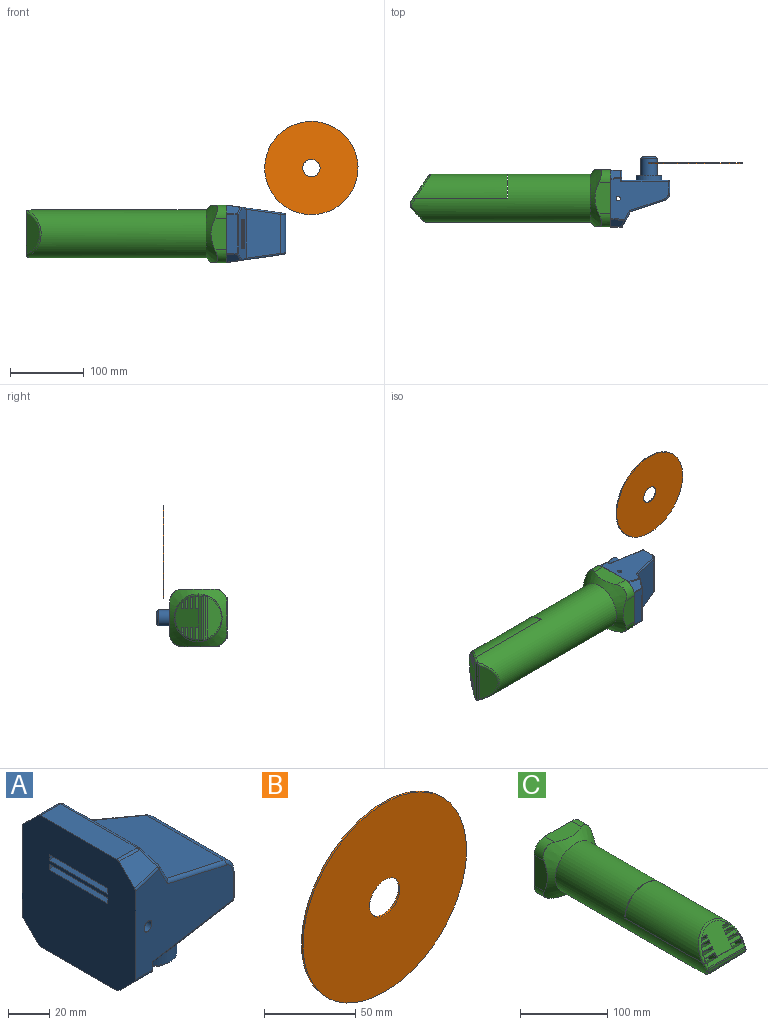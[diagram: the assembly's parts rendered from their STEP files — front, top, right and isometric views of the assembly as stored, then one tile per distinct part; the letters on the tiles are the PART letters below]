
ASSEMBLY  parts=3 mates=1
PART A: 66 faces, bbox 80.5x78.2x96.5 mm
  f0: plane 51.53x15.56mm, normal (1,0,0), area 801.8mm2, adj f22,f50,f56,f59
  f1: plane 68.69x20.14mm, normal (0.88,0,0.48), area 1249.5mm2, adj f4,f12,f13,f14,f15,f16,f17,f18
  f2: plane 70.22x12.02mm, normal (1,0,0), area 762.8mm2, adj f3,f33,f34,f44,f45,f49,f52,f55
  f3: plane 69.65x63mm, normal (0,0,-1), area 2855.1mm2, adj f2,f49,f55,f56,f61
  f4: plane 66.47x46.27mm, normal (0.32,0,0.95), area 2918.6mm2, adj f1,f22,f40,f54
  f5: plane 13x10.81mm, normal (0,-0.71,-0.71), area 181.5mm2, adj f7,f24,f34,f35
  f6: plane 18.33x10.81mm, normal (0,-0.71,0.71), area 219.9mm2, adj f7,f23,f25,f26
  f7: plane 78.03x78.03mm, normal (-1,0,0), area 5521.2mm2, adj f5,f6,f8,f9,f10,f11,f12,f13
  f8: plane 52.34x13.82mm, normal (0,0,1), area 723.3mm2, adj f7,f23,f30,f31
  f9: plane 52.34x13mm, normal (0,0,-1), area 680.5mm2, adj f7,f24,f32,f33
  f10: plane 13x10.81mm, normal (0,0.71,-0.71), area 181.5mm2, adj f7,f32,f43,f44
  f11: plane 18.33x10.81mm, normal (0,0.71,0.71), area 219.9mm2, adj f7,f31,f41,f42
  f12: plane 40x20.07mm, normal (0.48,0,-0.88), area 917.1mm2, adj f1,f7,f13,f15
  f13: plane 21.52x14.5mm, normal (0,1,0), area 71.3mm2, adj f1,f7,f12,f14
  f14: plane 40x21.52mm, normal (-0.48,0,0.88), area 983.3mm2, adj f1,f7,f13,f15
  f15: plane 21.52x14.5mm, normal (0,-1,0), area 71.3mm2, adj f1,f7,f12,f14
  f16: plane 40x22.47mm, normal (0.48,0,-0.88), area 1026.4mm2, adj f1,f7,f17,f19
  f17: plane 23.92x15.82mm, normal (0,1,0), area 79.5mm2, adj f1,f7,f16,f18
  f18: plane 40x23.92mm, normal (-0.48,0,0.88), area 1092.6mm2, adj f1,f7,f17,f19
  f19: plane 23.92x15.82mm, normal (0,-1,0), area 79.5mm2, adj f1,f7,f16,f18
  f20: plane 78.47x57.07mm, normal (0.14,0.99,0), area 2906.3mm2, adj f7,f42,f43,f51,f52,f54,f55,f57
  f21: plane 78.28x56.89mm, normal (0.14,-0.99,0), area 2906.3mm2, adj f7,f25,f35,f36,f40,f45,f46,f49
  f22: cylinder r=10.34mm len=53.17mm, axis (0,1,0), area 672.2mm2, adj f0,f4,f46,f57
  f23: cylinder r=2mm len=13.82mm, axis (1,0,0), area 21.7mm2, adj f6,f7,f8,f27
  f24: cylinder r=2mm len=13mm, axis (-1,0,0), area 20.4mm2, adj f5,f7,f9,f28
  f25: cylinder r=2mm len=18.9mm, axis (0.98,0.14,0.14), area 30mm2, adj f6,f7,f21,f29
  f26: cylinder r=2mm len=9.59mm, axis (-0.36,0.66,0.66), area 30.3mm2, adj f1,f6,f27,f29
  f27: sphere r=2mm, area 1.9mm2, adj f23,f26,f30
  f28: sphere r=2mm, area 3.1mm2, adj f24,f33,f34
  f29: sphere r=2mm, area 2.4mm2, adj f25,f26,f36
  f30: cylinder r=2mm len=52.34mm, axis (0,1,0), area 111.7mm2, adj f1,f8,f27,f37
  f31: cylinder r=2mm len=13.82mm, axis (1,0,0), area 21.7mm2, adj f7,f8,f11,f37
  f32: cylinder r=2mm len=13mm, axis (-1,0,0), area 20.4mm2, adj f7,f9,f10,f38
  f33: cylinder r=2mm len=52.34mm, axis (0,1,0), area 164.4mm2, adj f2,f9,f28,f38
  f34: cylinder r=2mm len=10.35mm, axis (0,-0.71,0.71), area 39.7mm2, adj f2,f5,f28,f39
  f35: cylinder r=2mm len=13.57mm, axis (0.98,0.14,-0.14), area 21.3mm2, adj f5,f7,f21,f39
  f36: cylinder r=2mm len=13.6mm, axis (0.48,0.07,-0.87), area 40.5mm2, adj f1,f21,f29,f40
  f37: sphere r=2mm, area 1.9mm2, adj f30,f31,f41
  f38: sphere r=2mm, area 3.1mm2, adj f32,f33,f44
  f39: sphere r=2mm, area 2.9mm2, adj f34,f35,f45
  f40: cylinder r=2mm len=47.41mm, axis (0.94,0.14,-0.31), area 151.2mm2, adj f1,f4,f21,f36,f46
  f41: cylinder r=2mm len=9.59mm, axis (-0.36,-0.66,0.66), area 30.3mm2, adj f1,f11,f37,f47
  f42: cylinder r=2mm len=18.9mm, axis (0.98,-0.14,0.14), area 30mm2, adj f7,f11,f20,f47
  f43: cylinder r=2mm len=13.57mm, axis (0.98,-0.14,-0.14), area 21.3mm2, adj f7,f10,f20,f48
  f44: cylinder r=2mm len=10.35mm, axis (0,0.71,0.71), area 39.7mm2, adj f2,f10,f38,f48
  f45: cylinder r=2mm len=5.06mm, axis (0,0,-1), area 11mm2, adj f2,f21,f39,f49
  f46: bspline ~9.8x7.41mm, area 35mm2, adj f21,f22,f40,f50
  f47: sphere r=2mm, area 2.4mm2, adj f41,f42,f51
  f48: sphere r=2mm, area 2.9mm2, adj f43,f44,f52
  f49: cylinder r=2mm len=65.28mm, axis (-0.99,-0.14,0), area 202.3mm2, adj f2,f3,f21,f45,f53
  f50: cylinder r=2mm len=15.56mm, axis (0,0,-1), area 44.4mm2, adj f0,f21,f46,f53
  f51: cylinder r=2mm len=13.6mm, axis (-0.48,0.07,0.87), area 40.5mm2, adj f1,f20,f47,f54
  f52: cylinder r=2mm len=5.06mm, axis (0,0,1), area 11mm2, adj f2,f20,f48,f55
  f53: sphere r=2mm, area 5.7mm2, adj f49,f50,f56
  f54: cylinder r=2mm len=47.41mm, axis (-0.94,0.14,0.31), area 151.2mm2, adj f1,f4,f20,f51,f57
  f55: cylinder r=2mm len=65.28mm, axis (0.99,-0.14,0), area 202.3mm2, adj f2,f3,f20,f52,f58
  f56: cylinder r=2mm len=51.53mm, axis (0,-1,0), area 161.9mm2, adj f0,f3,f53,f58
  f57: bspline ~9.8x7.41mm, area 35mm2, adj f20,f22,f54,f59
  f58: sphere r=2mm, area 5.7mm2, adj f55,f56,f59
  f59: cylinder r=2mm len=15.56mm, axis (0,0,1), area 44.4mm2, adj f0,f20,f57,f58
  f60: cylinder r=3.04mm len=76.01mm, axis (0,1,0), area 1434.7mm2, adj f20,f21
  f61: cylinder r=17.5mm len=35mm, axis (0,0,1), area 769.7mm2, adj f3,f62
  f62: plane 35x35mm, normal (0,0,-1), area 582mm2, adj f61,f63
  f63: cylinder r=11mm len=23.3mm, axis (0,0,1), area 1610.4mm2, adj f62,f65
  f64: plane 18x18mm, normal (0,0,-1), area 254.5mm2, adj f65
  f65: cone r=9mm half-angle=45deg, axis (0,0,1), area 177.7mm2, adj f63,f64
PART B: 4 faces, bbox 126.9x1.2x126.9 mm
  f0: cylinder r=11.79mm len=23.58mm, axis (0,1,0), area 88.9mm2, adj f2,f3
  f1: cylinder r=63.44mm len=126.87mm, axis (0,1,0), area 478.3mm2, adj f2,f3
  f2: plane 126.87x126.87mm, normal (0,-1,0), area 12205.9mm2, adj f0,f1
  f3: plane 126.87x126.87mm, normal (0,1,0), area 12205.9mm2, adj f0,f1
PART C: 123 faces, bbox 95.5x277.8x95.5 mm
  f0: plane 58.88x5.05mm, normal (0,-0.82,0.57), area 333.3mm2, adj f1,f2,f9,f11,f23,f35,f46,f111
  f1: bspline ~16.85x12.86mm, area 47.4mm2, adj f0,f10,f18,f19,f22,f23,f46,f111
  f2: bspline ~16.85x12.86mm, area 47.4mm2, adj f0,f12,f18,f19,f22,f23,f35,f111
  f3: cylinder r=42.74mm len=15.09mm, axis (0,-0.82,0.57), area 67.1mm2, adj f4,f12,f35,f39,f111
  f4: plane 16.41x6.55mm, normal (0,-0.57,-0.82), area 131.3mm2, adj f3,f5,f39,f111
  f5: plane 15.13x9.21mm, normal (1,0,0), area 67.1mm2, adj f4,f11,f35,f39,f111
  f6: cylinder r=42.74mm len=15.09mm, axis (0,-0.82,0.57), area 67.1mm2, adj f8,f10,f46,f49,f111
  f7: plane 15.13x9.21mm, normal (-1,0,0), area 67.1mm2, adj f8,f9,f46,f49,f111
  f8: plane 16.41x6.55mm, normal (0,-0.57,-0.82), area 131.3mm2, adj f6,f7,f49,f111
  f9: cylinder r=0.48mm len=1.16mm, axis (0,0.57,0.82), area 0.7mm2, adj f0,f7,f46,f111
  f10: bspline ~4.96x3.72mm, area 0.8mm2, adj f1,f6,f46,f111
  f11: cylinder r=0.48mm len=1.16mm, axis (0,-0.57,-0.82), area 0.7mm2, adj f0,f5,f35,f111
  f12: bspline ~4.96x3.72mm, area 0.8mm2, adj f2,f3,f35,f111
  f13: plane 58.81x31.18mm, normal (0,-0.82,0.57), area 1321.5mm2, adj f14,f43,f51,f58,f63,f68,f71,f75
  f14: bspline ~65x34.27mm, area 379.4mm2, adj f13,f18,f43,f51,f58,f63,f68,f71
  f15: plane 6.23x6.23mm, normal (0,-1,0), area 2.1mm2, adj f31,f34
  f16: plane 6.23x6.23mm, normal (0,-1,0), area 2.1mm2, adj f30,f34
  f17: plane 6.23x6.23mm, normal (0,-1,0), area 2.1mm2, adj f33,f34
  f18: cylinder r=32.5mm len=243.48mm, axis (0,1,0), area 46579.7mm2, adj f1,f2,f14,f22,f34,f109,f110,f111
  f19: plane 61.71x3.98mm, normal (0,-1,0), area 226.9mm2, adj f1,f2,f21,f22,f23
  f20: plane 55.12x18.98mm, normal (0,-0.73,-0.68), area 1034.3mm2, adj f21,f22
  f21: cylinder r=3mm len=60.35mm, axis (1,0,0), area 129.2mm2, adj f19,f20,f22
  f22: bspline ~62.38x23.36mm, area 276.2mm2, adj f1,f2,f18,f19,f20,f21
  f23: cylinder r=3mm len=60.2mm, axis (-1,0,0), area 107.7mm2, adj f0,f1,f2,f19
  f24: plane 42.75x21.71mm, normal (1,0,0), area 847.7mm2, adj f28,f30,f33,f34
  f25: plane 42.75x21.71mm, normal (0,0,1), area 847.7mm2, adj f28,f30,f31,f34
  f26: plane 42.75x21.71mm, normal (-1,0,0), area 847.7mm2, adj f28,f31,f32,f34
  f27: plane 42.75x21.71mm, normal (0,0,-1), area 847.7mm2, adj f28,f32,f33,f34
  f28: plane 78x78mm, normal (0,1,0), area 5817.4mm2, adj f24,f25,f26,f27,f30,f31,f32,f33
  f29: plane 6.23x6.23mm, normal (0,-1,0), area 2.1mm2, adj f32,f34
  f30: cylinder r=17.62mm len=17.62mm, axis (0,1,0), area 393.8mm2, adj f16,f24,f25,f28,f34
  f31: cylinder r=17.62mm len=17.62mm, axis (0,-1,0), area 393.8mm2, adj f15,f25,f26,f28,f34
  f32: cylinder r=17.62mm len=17.62mm, axis (0,1,0), area 393.8mm2, adj f26,f27,f28,f29,f34
  f33: cylinder r=17.62mm len=17.62mm, axis (0,-1,0), area 393.8mm2, adj f17,f24,f27,f28,f34
  f34: cone r=32.5mm half-angle=45deg, axis (0,1,0), area 3495.9mm2, adj f15,f16,f17,f18,f24,f25,f26,f27
  f35: plane 17.5x12.31mm, normal (0,0.57,0.82), area 246.3mm2, adj f0,f2,f3,f5,f11,f12,f39
  f36: cylinder r=42.74mm len=7.69mm, axis (0,-0.82,0.57), area 13.9mm2, adj f37,f83,f84,f110
  f37: plane 16.41x5.2mm, normal (0,-0.57,-0.82), area 104.1mm2, adj f36,f38,f81,f82,f84,f110
  f38: plane 7.75x3.64mm, normal (1,0,0), area 14.1mm2, adj f37,f80,f110
  f39: plane 16.51x4.62mm, normal (0,-0.82,0.57), area 93mm2, adj f3,f4,f5,f35
  f40: cylinder r=28.27mm len=13.96mm, axis (0,-0.82,0.57), area 58.5mm2, adj f41,f43,f44,f92
  f41: plane 11.94x11.89mm, normal (0,-0.57,-0.82), area 173.3mm2, adj f40,f42,f44,f90,f91,f92
  f42: plane 14x11.34mm, normal (1,0,0), area 53.4mm2, adj f41,f43,f44,f89
  f43: plane 14.71x12.3mm, normal (0,0.57,0.82), area 204.2mm2, adj f13,f14,f40,f42,f44,f89,f92
  f44: plane 13.6x3.01mm, normal (0,-0.82,0.57), area 47.1mm2, adj f40,f41,f42,f43
  f45: cylinder r=42.74mm len=7.69mm, axis (0,-0.82,0.57), area 13.9mm2, adj f48,f78,f79,f110
  f46: plane 17.5x12.31mm, normal (0,0.57,0.82), area 246.3mm2, adj f0,f1,f6,f7,f9,f10,f49
  f47: plane 7.75x3.64mm, normal (-1,0,0), area 14.1mm2, adj f48,f75,f110
  f48: plane 16.41x5.2mm, normal (0,-0.57,-0.82), area 104.1mm2, adj f45,f47,f76,f77,f79,f110
  f49: plane 16.51x4.62mm, normal (0,-0.82,0.57), area 93mm2, adj f6,f7,f8,f46
  f50: cylinder r=28.27mm len=13.96mm, axis (0,-0.82,0.57), area 58.5mm2, adj f51,f53,f54,f88
  f51: plane 14.71x12.3mm, normal (0,0.57,0.82), area 204.2mm2, adj f13,f14,f50,f52,f54,f85,f88
  f52: plane 14x11.34mm, normal (-1,0,0), area 53.4mm2, adj f51,f53,f54,f85
  f53: plane 11.94x11.89mm, normal (0,-0.57,-0.82), area 173.3mm2, adj f50,f52,f54,f86,f87,f88
  f54: plane 13.6x3.01mm, normal (0,-0.82,0.57), area 47.1mm2, adj f50,f51,f52,f53
  f55: plane 13.66x10.09mm, normal (-1,0,0), area 44.1mm2, adj f56,f58,f59,f105,f110
  f56: plane 15.19x11.89mm, normal (0,-0.57,-0.82), area 220.5mm2, adj f55,f57,f59,f106,f107,f108
  f57: cylinder r=94.57mm len=13.62mm, axis (0,-0.82,0.57), area 44.9mm2, adj f56,f58,f59,f106,f110
  f58: plane 16.92x11.22mm, normal (0,0.57,0.82), area 216.8mm2, adj f13,f14,f55,f57,f105,f106,f110
  f59: plane 15.66x1.77mm, normal (0,-0.82,0.57), area 33.2mm2, adj f55,f56,f57,f110
  f60: cylinder r=33.17mm len=13.66mm, axis (0,-0.82,0.57), area 56.8mm2, adj f61,f63,f64,f94
  f61: plane 11.89x8.33mm, normal (0,-0.57,-0.82), area 109.6mm2, adj f60,f62,f64,f94,f95,f96
  f62: plane 13.69x10.9mm, normal (1,0,0), area 45.6mm2, adj f61,f63,f64,f93
  f63: plane 12.3x11.08mm, normal (0,0.57,0.82), area 148.7mm2, adj f13,f14,f60,f62,f64,f93,f94
  f64: plane 9.9x2.57mm, normal (0,-0.82,0.57), area 27.6mm2, adj f60,f61,f62,f63
  f65: cylinder r=94.57mm len=13.62mm, axis (0,-0.82,0.57), area 44.9mm2, adj f66,f68,f69,f101,f110
  f66: plane 15.19x11.89mm, normal (0,-0.57,-0.82), area 220.5mm2, adj f65,f67,f69,f101,f102,f103
  f67: plane 13.66x10.09mm, normal (1,0,0), area 44.1mm2, adj f66,f68,f69,f104,f110
  f68: plane 16.92x11.22mm, normal (0,0.57,0.82), area 216.8mm2, adj f13,f14,f65,f67,f101,f104,f110
  f69: plane 15.66x1.77mm, normal (0,-0.82,0.57), area 33.2mm2, adj f65,f66,f67,f110
  f70: cylinder r=33.17mm len=13.66mm, axis (0,-0.82,0.57), area 56.8mm2, adj f71,f73,f74,f98
  f71: plane 12.3x11.08mm, normal (0,0.57,0.82), area 148.7mm2, adj f13,f14,f70,f72,f74,f97,f98
  f72: plane 13.69x10.9mm, normal (-1,0,0), area 45.6mm2, adj f71,f73,f74,f97
  f73: plane 11.89x8.33mm, normal (0,-0.57,-0.82), area 109.6mm2, adj f70,f72,f74,f98,f99,f100
  f74: plane 9.9x2.57mm, normal (0,-0.82,0.57), area 27.6mm2, adj f70,f71,f72,f73
  f75: cylinder r=0.48mm len=4.59mm, axis (0,0.57,0.82), area 3.7mm2, adj f13,f47,f76,f110
  f76: cylinder r=0.48mm len=16.86mm, axis (-1,0,0), area 12.6mm2, adj f13,f48,f75,f77
  f77: bspline ~1.42x0.76mm, area 0.2mm2, adj f14,f48,f76,f79
  f78: bspline ~7x5.14mm, area 3.1mm2, adj f14,f45,f79,f110
  f79: bspline ~6.99x5.14mm, area 0.9mm2, adj f14,f45,f48,f77,f78
  f80: cylinder r=0.48mm len=4.59mm, axis (0,-0.57,-0.82), area 3.7mm2, adj f13,f38,f81,f110
  f81: cylinder r=0.48mm len=16.86mm, axis (-1,0,0), area 12.6mm2, adj f13,f37,f80,f82
  f82: bspline ~1.42x0.76mm, area 0.2mm2, adj f14,f37,f81,f84
  f83: bspline ~7x5.14mm, area 3.1mm2, adj f14,f36,f84,f110
  f84: bspline ~6.99x5.14mm, area 0.9mm2, adj f14,f36,f37,f82,f83
  f85: cylinder r=0.48mm len=3.68mm, axis (0,0.57,0.82), area 3mm2, adj f13,f51,f52,f86
  f86: cylinder r=0.48mm len=12.17mm, axis (-1,0,0), area 9mm2, adj f13,f53,f85,f87
  f87: bspline ~1.69x0.79mm, area 0.3mm2, adj f14,f53,f86,f88
  f88: bspline ~5.97x4.3mm, area 3.6mm2, adj f14,f50,f51,f53,f87
  f89: cylinder r=0.48mm len=3.68mm, axis (0,-0.57,-0.82), area 3mm2, adj f13,f42,f43,f90
  f90: cylinder r=0.48mm len=12.17mm, axis (-1,0,0), area 9mm2, adj f13,f41,f89,f91
  f91: bspline ~1.69x0.79mm, area 0.3mm2, adj f14,f41,f90,f92
  f92: bspline ~6.7x4.77mm, area 3.6mm2, adj f14,f40,f41,f43,f91
  f93: cylinder r=0.48mm len=3.24mm, axis (0,-0.57,-0.82), area 2.6mm2, adj f13,f62,f63,f95
  f94: bspline ~5.25x4.81mm, area 3.5mm2, adj f14,f60,f61,f63,f96
  f95: cylinder r=0.48mm len=7.62mm, axis (-1,0,0), area 5.6mm2, adj f13,f61,f93,f96
  f96: bspline ~1.92x0.8mm, area 0.4mm2, adj f14,f61,f94,f95
  f97: cylinder r=0.48mm len=3.24mm, axis (0,0.57,0.82), area 2.6mm2, adj f13,f71,f72,f99
  f98: bspline ~4.98x4.5mm, area 3.5mm2, adj f14,f70,f71,f73,f100
  f99: cylinder r=0.48mm len=7.62mm, axis (-1,0,0), area 5.6mm2, adj f13,f73,f97,f100
  f100: bspline ~1.92x0.8mm, area 0.4mm2, adj f14,f73,f98,f99
  f101: bspline ~6.18x4.55mm, area 2.8mm2, adj f14,f65,f66,f68,f102
  f102: bspline ~1.5x0.76mm, area 0.2mm2, adj f14,f66,f101,f103
  f103: cylinder r=0.48mm len=15.54mm, axis (-1,0,0), area 11.6mm2, adj f13,f66,f102,f104
  f104: cylinder r=0.48mm len=3.2mm, axis (0,-0.57,-0.82), area 2.5mm2, adj f13,f67,f68,f103
  f105: cylinder r=0.48mm len=3.2mm, axis (0,0.57,0.82), area 2.5mm2, adj f13,f55,f58,f107
  f106: bspline ~6.35x4.67mm, area 2.8mm2, adj f14,f56,f57,f58,f108
  f107: cylinder r=0.48mm len=15.54mm, axis (-1,0,0), area 11.6mm2, adj f13,f56,f105,f108
  f108: bspline ~1.5x0.76mm, area 0.2mm2, adj f14,f56,f106,f107
  f109: plane 65x0.1mm, normal (0,-1,0), area 6.5mm2, adj f18,f110,f111
  f110: plane 128.39x65.45mm, normal (0,0,-1), area 7985.5mm2, adj f13,f14,f18,f36,f37,f38,f45,f47
  f111: plane 128.46x65.45mm, normal (0,0,1), area 7989.7mm2, adj f0,f1,f2,f3,f4,f5,f6,f7
  f112: plane 15.84x0.66mm, normal (0,-0.82,0.57), area 12.7mm2, adj f111,f113,f114,f115
  f113: plane 15.84x0.94mm, normal (0,0.57,0.82), area 18.2mm2, adj f111,f112,f114,f115
  f114: plane 1.4x0.66mm, normal (1,0,0), area 0.5mm2, adj f111,f112,f113
  f115: cylinder r=94.57mm len=1.4mm, axis (0,-0.82,0.57), area 0.5mm2, adj f111,f112,f113
  f116: plane 15.84x0.66mm, normal (0,-0.82,0.57), area 12.7mm2, adj f111,f117,f118,f119
  f117: plane 15.84x0.94mm, normal (0,0.57,0.82), area 18.2mm2, adj f111,f116,f118,f119
  f118: cylinder r=94.57mm len=1.4mm, axis (0,-0.82,0.57), area 0.5mm2, adj f111,f116,f117
  f119: plane 1.4x0.66mm, normal (-1,0,0), area 0.5mm2, adj f111,f116,f117
  f120: plane 65x0.6mm, normal (0,0,1), area 39mm2, adj f18,f121,f122
  f121: plane 65x32.5mm, normal (0,1,0), area 1659.2mm2, adj f18,f120
  f122: plane 65x32.5mm, normal (0,-1,0), area 1659.2mm2, adj f18,f120
PLACE A rot(axis=(1,0,0),90deg) t=(-203.51,27.18,-85.16)mm
PLACE B t=(-88.6,75.7,4.33)mm
PLACE C rot(axis=(-0.58,-0.58,-0.58),120deg) t=(-216.71,27.88,-85.16)mm
MATE fastened A.f7 <-> C.f18  axis (-1,0,0) through (-203.51,27.88,-85.16)mm
